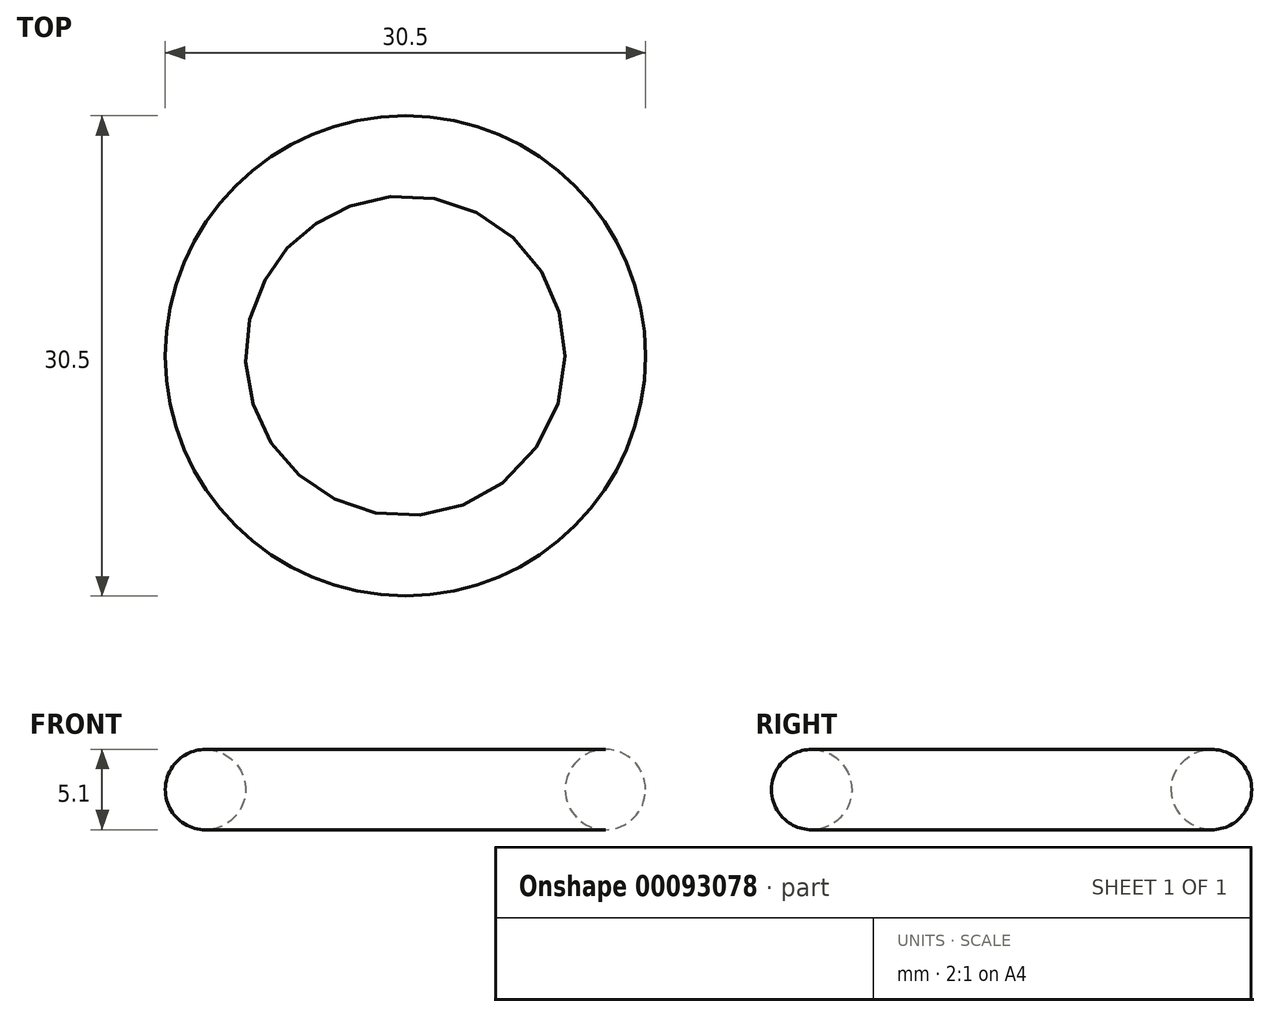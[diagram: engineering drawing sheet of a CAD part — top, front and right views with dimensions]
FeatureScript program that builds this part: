
annotation { "Feature Type Name" : "Feature", "Feature Type Description" : "" }
export const myFeature = defineFeature(function(context is Context, id is Id, definition is map)
    precondition{}
    {
        {
            var Q0;
            Q0=qCreatedBy(makeId("Front.planeOp"),FACE);
            var sketch = newSketch(context, id + "F0", { "sketchPlane" : qUnion([Q0])});
            skCircle(sketch, "E0", {"center": v(12.7, 0) * mm, "radius": 2.55 * mm});
            skLineSegment(sketch, "E1", {"start": v(0, 56) * mm, "end": v(0, -27.6) * mm});
            skSolve(sketch);
        }
        {
            var Q0;
            Q0=makeQuery(id+"F0.imprint","IMPRINT",FACE,{"disambiguationData":[TD([[makeQuery(id+"F0.imprint","IMPRINT",EDGE,{"derivedFrom":sQuery(id+"F0.wireOp",EDGE,"E0")}),1.0]])]});
            var Q1;
            Q1=sQuery(id+"F0.wireOp",EDGE,"E0");
            var Q2;
            Q2=sQuery(id+"F0.wireOp",EDGE,"E1");
            revolve(context, id + "F1", {"entities" : qUnion([Q0]), "surfaceEntities" : qUnion([Q1]), "axis" : qUnion([Q2]), "revolveType" : RevolveType.FULL});
        }
    });
